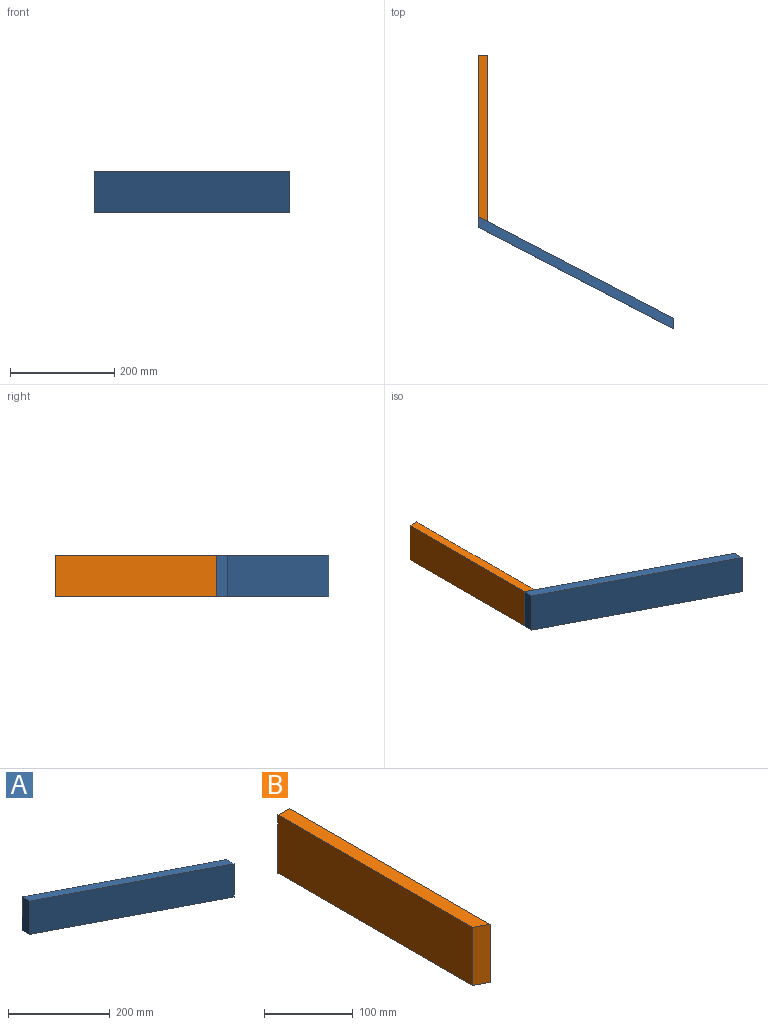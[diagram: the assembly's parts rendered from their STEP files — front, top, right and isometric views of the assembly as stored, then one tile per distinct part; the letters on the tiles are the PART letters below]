
ASSEMBLY  parts=2 mates=1
PART A: 6 faces, bbox 375x215.1x80 mm
  f0: plane 80x20.28mm, normal (-1,0,0), area 1622.7mm2, adj f1,f3,f4,f5
  f1: plane 375x194.81mm, normal (-0.46,-0.89,0), area 33806.4mm2, adj f0,f2,f4,f5
  f2: plane 80x20.28mm, normal (1,0,0), area 1622.7mm2, adj f1,f3,f4,f5
  f3: plane 375x194.81mm, normal (0.46,0.89,0), area 33806.4mm2, adj f0,f2,f4,f5
  f4: plane 375x215.09mm, normal (0,0,1), area 7606.4mm2, adj f0,f1,f2,f3
  f5: plane 375x215.09mm, normal (0,0,-1), area 7606.4mm2, adj f0,f1,f2,f3
PART B: 6 faces, bbox 18x319.1x80 mm
  f0: plane 80x18mm, normal (0,1,0), area 1440mm2, adj f1,f3,f4,f5
  f1: plane 309.72x80mm, normal (-1,0,0), area 24777.3mm2, adj f0,f2,f4,f5
  f2: plane 80x18mm, normal (-0.46,-0.89,0), area 1622.7mm2, adj f1,f3,f4,f5
  f3: plane 319.07x80mm, normal (1,0,0), area 25525.3mm2, adj f0,f2,f4,f5
  f4: plane 319.07x18mm, normal (0,0,1), area 5659mm2, adj f0,f1,f2,f3
  f5: plane 319.07x18mm, normal (0,0,-1), area 5659mm2, adj f0,f1,f2,f3
PLACE A t=(-46.57,-36.4,-57.7)mm
PLACE B t=(-46.57,169.33,-57.7)mm
MATE planar B.f2 <-> A.f3  axis (-0.46,-0.89,0) through (-46.57,178.68,22.3)mm
